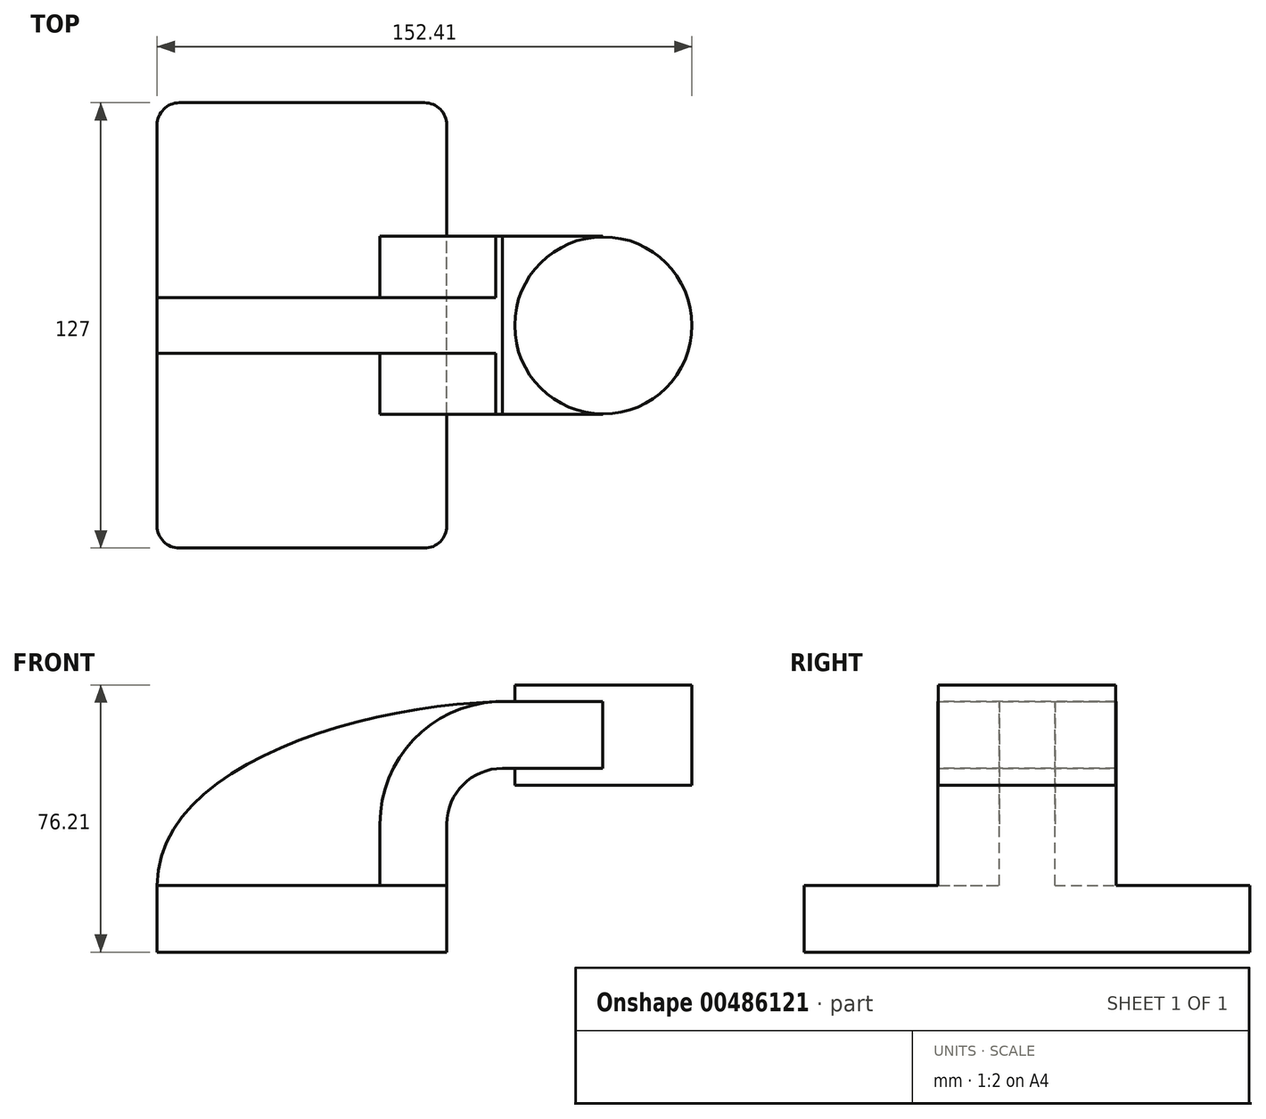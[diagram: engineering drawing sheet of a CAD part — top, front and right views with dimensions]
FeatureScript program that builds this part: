
annotation { "Feature Type Name" : "Feature", "Feature Type Description" : "" }
export const myFeature = defineFeature(function(context is Context, id is Id, definition is map)
    precondition{}
    {
        {
            var Q0;
            Q0=qCreatedBy(makeId("Front.planeOp"),FACE);
            var sketch = newSketch(context, id + "F0", { "sketchPlane" : qUnion([Q0])});
            skLineSegment(sketch, "E0.bottom", {"start": v(41.28, -9.52) * mm, "end": v(-41.28, -9.53) * mm});
            skLineSegment(sketch, "E0.top", {"start": v(41.28, 9.53) * mm, "end": v(-41.28, 9.52) * mm});
            skLineSegment(sketch, "E0.left", {"start": v(41.28, -9.52) * mm, "end": v(41.28, 9.53) * mm});
            skLineSegment(sketch, "E0.right", {"start": v(-41.28, -9.53) * mm, "end": v(-41.28, 9.52) * mm});
            skPoint(sketch, "E0.middle", {"position": v(0, 0) * mm});
            skLineSegment(sketch, "E1.bottom", {"start": v(60.32, 66.68) * mm, "end": v(111.12, 66.68) * mm});
            skLineSegment(sketch, "E1.top", {"start": v(60.32, 38.1) * mm, "end": v(111.12, 38.1) * mm});
            skLineSegment(sketch, "E1.left", {"start": v(60.32, 66.68) * mm, "end": v(60.32, 38.1) * mm});
            skLineSegment(sketch, "E1.right", {"start": v(111.12, 66.68) * mm, "end": v(111.12, 38.1) * mm});
            skPoint(sketch, "E1.middle", {"position": v(85.72, 52.39) * mm});
            skPoint(sketch, "E2.endSnap0", {"position": v(60.32, 52.39) * mm});
            skLineSegment(sketch, "E3", {"start": v(41.28, 9.53) * mm, "end": v(41.28, 27) * mm});
            skArc(sketch, "E4", {"start": v(41.28, 27) * mm, "mid": v(45.92, 38.23) * mm, "end": v(57.15, 42.88) * mm});
            skLineSegment(sketch, "E5", {"start": v(57.15, 42.88) * mm, "end": v(85.72, 42.88) * mm});
            skArc(sketch, "E6.0", {"start": v(22.23, 27) * mm, "mid": v(32.45, 51.7) * mm, "end": v(57.15, 61.93) * mm});
            skLineSegment(sketch, "E6.1", {"start": v(22.23, 9.53) * mm, "end": v(22.23, 27) * mm});
            skLineSegment(sketch, "E7", {"start": v(57.15, 61.93) * mm, "end": v(85.72, 61.93) * mm});
            skLineSegment(sketch, "E8", {"start": v(85.72, 61.93) * mm, "end": v(85.72, 42.88) * mm});
            skFitSpline(sketch, "E9", {"points": [v(-41.28, 9.52) * mm, v(57.15, 61.93) * mm], "startDerivative": vector(-0.18, 101.21) * mm, "endDerivative": vector(124.42, 2.74) * mm});
            skSolve(sketch);
        }
        {
            var Q0;
            Q0=makeQuery(id+"F0.imprint","IMPRINT",FACE,{"disambiguationData":[TD([[makeQuery(id+"F0.imprint","IMPRINT",EDGE,{"derivedFrom":sQuery(id+"F0.wireOp",EDGE,"E0.bottom")}),-1.0]])]});
            extrude(context, id + "F1", {"entities" : qUnion([Q0]), "depth" : 127 * mm, "symmetric" : true});
        }
        {
            var Q0;
            {var subQ1=sQuery(id+"F0.wireOp",EDGE,"E3");Q0=makeQuery(id+"F0.imprint","IMPRINT",FACE,{"disambiguationData":[TD([[makeQuery(id+"F0.imprint","IMPRINT",EDGE,{"derivedFrom":subQ1}),1.0]])]});}
            var Q1;
            {var subQ5=sQuery(id+"F0.wireOp",EDGE,"E8");Q1=makeQuery(id+"F0.imprint","IMPRINT",FACE,{"disambiguationData":[TD([[makeQuery(id+"F0.imprint","IMPRINT",EDGE,{"derivedFrom":subQ5}),-1.0]])]});}
            extrude(context, id + "F2", {"entities" : qUnion([Q0, Q1]), "operationType" : NewBodyOperationType.ADD, "depth" : 50.8 * mm, "symmetric" : true});
        }
        {
            var Q0;
            {var subQ3=sQuery(id+"F0.wireOp",EDGE,"E6.1");Q0=makeQuery(id+"F0.imprint","IMPRINT",FACE,{"disambiguationData":[TD([[makeQuery(id+"F0.imprint","IMPRINT",EDGE,{"derivedFrom":subQ3}),1.0]])]});}
            extrude(context, id + "F3", {"entities" : qUnion([Q0]), "operationType" : NewBodyOperationType.ADD, "oppositeDirection" : true, "depth" : 15.88 * mm, "symmetric" : true});
        }
        {
            var Q0;
            {var subQ5=sQuery(id+"F0.wireOp",EDGE,"E1.bottom");Q0=makeQuery(id+"F0.imprint","IMPRINT",FACE,{"disambiguationData":[TD([[makeQuery(id+"F0.imprint","IMPRINT",EDGE,{"derivedFrom":subQ5}),-1.0]])]});}
            var sketch = newSketch(context, id + "F4", { "sketchPlane" : qUnion([Q0])});
            skLineSegment(sketch, "E10", {"start": v(85.87, 43.08) * mm, "end": v(85.87, 66.94) * mm});
            skLineSegment(sketch, "E11", {"start": v(85.87, 66.94) * mm, "end": v(85.87, 37.77) * mm});
            skSolve(sketch);
        }
        {
            var Q0;
            {var subQ0=makeQuery(id+"F0.imprint","IMPRINT",EDGE,{"derivedFrom":sQuery(id+"F0.wireOp",EDGE,"E1.right")});Q0=makeQuery(id+"F4.imprint","IMPRINT",FACE,{"disambiguationData":[TD([[makeQuery(id+"F4.imprint","IMPRINT",EDGE,{"derivedFrom":subQ0}),-1.0]])]});}
            var Q1;
            Q1=sQuery(id+"F4.wireOp",EDGE,"E11");
            revolve(context, id + "F5", {"operationType" : NewBodyOperationType.ADD, "surfaceOperationType" : NewSurfaceOperationType.NEW, "entities" : qUnion([Q0]), "axis" : qUnion([Q1]), "revolveType" : RevolveType.FULL});
        }
        {
            var Q0;
            Q0=makeQuery(id+"F1.opExtrude","CAP_EDGE",EDGE,{"disambiguationData":[OSD([sQuery(id+"F0.wireOp",EDGE,"E0.left")])],"isStart":true});
            var Q1;
            Q1=makeQuery(id+"F1.opExtrude","CAP_EDGE",EDGE,{"disambiguationData":[OSD([sQuery(id+"F0.wireOp",EDGE,"E0.left")])],"isStart":false});
            var Q2;
            Q2=makeQuery(id+"F1.opExtrude","CAP_EDGE",EDGE,{"disambiguationData":[OSD([sQuery(id+"F0.wireOp",EDGE,"E0.right")])],"isStart":true});
            var Q3;
            Q3=makeQuery(id+"F1.opExtrude","CAP_EDGE",EDGE,{"disambiguationData":[OSD([sQuery(id+"F0.wireOp",EDGE,"E0.right")])],"isStart":false});
            fillet(context, id + "F6", {"entities" : qUnion([Q0, Q1, Q2, Q3]), "radius" : 6.35 * mm, "tangentPropagation" : true, "allowEdgeOverflow" : false});
        }
    });
